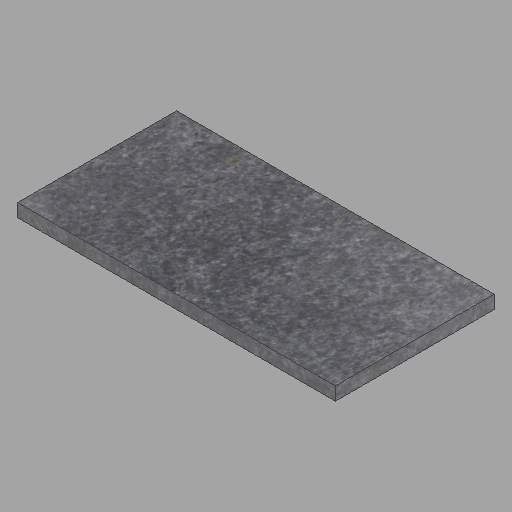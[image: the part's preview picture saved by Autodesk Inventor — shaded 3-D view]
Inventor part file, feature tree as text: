
AUTODESK INVENTOR PART (.ipt)
format: ipt  version: 2023 (Build 270158000, 158)  size: 221,696 bytes
history: native  units: in
note: dims shown in document units (in); Inventor stores cm internally (conversion verified against a paired STEP export)
features: other x1, extrude x1, sketch x1
ambient origin geometry x8: Origin, YZ Plane, XZ Plane, XY Plane, X Axis, Y Axis, Z Axis, Center Point
bodies: Solid1 (feature_tree)
feature tree (3):
  other  "2x24x48-26"
  extrude  "Extrusion1"  Depth=24.0in
  sketch  "Sketch1"  dims[d0=2.0in d1=24.0in d2=48.0in d3=0.0in]
